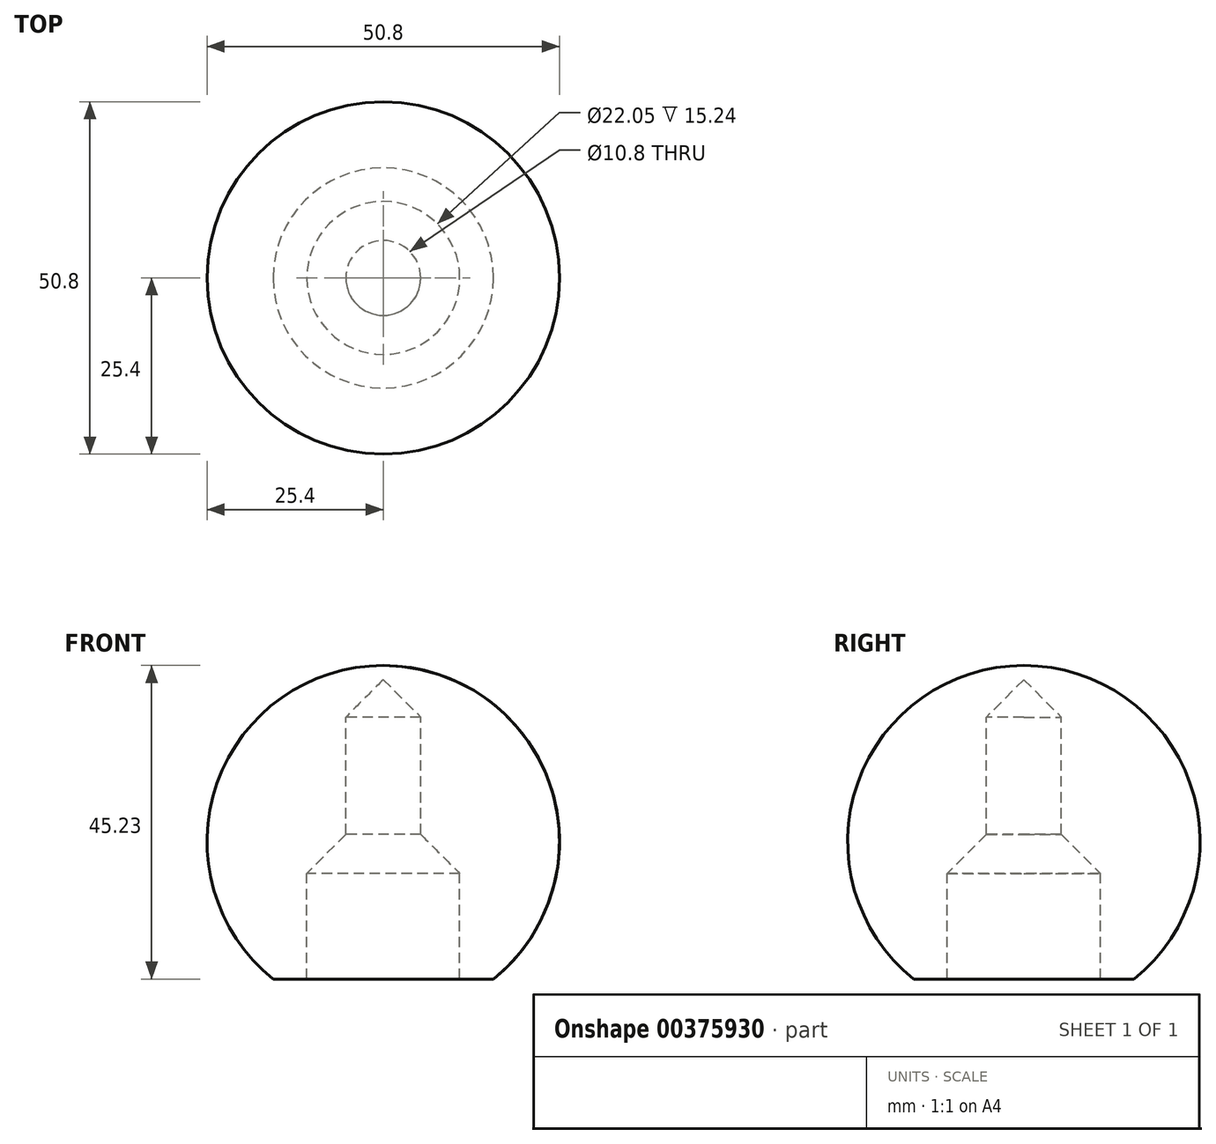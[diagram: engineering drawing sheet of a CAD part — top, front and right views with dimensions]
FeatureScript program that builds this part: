
annotation { "Feature Type Name" : "Feature", "Feature Type Description" : "" }
export const myFeature = defineFeature(function(context is Context, id is Id, definition is map)
    precondition{}
    {
        {
            var Q0;
            Q0=qCreatedBy(makeId("Front.planeOp"),FACE);
            var sketch = newSketch(context, id + "F0", { "sketchPlane" : qUnion([Q0])});
            skLineSegment(sketch, "E0", {"start": v(0, 0) * mm, "end": v(15.88, 0) * mm});
            skLineSegment(sketch, "E1", {"start": v(0, 0) * mm, "end": v(0, 45.23) * mm});
            skArc(sketch, "E2", {"start": v(15.88, 0) * mm, "mid": v(23.97, 28.24) * mm, "end": v(0, 45.23) * mm});
            skSolve(sketch);
        }
        {
            var Q0;
            Q0=makeQuery(id+"F0.imprint","IMPRINT",FACE,{"disambiguationData":[TD([[makeQuery(id+"F0.imprint","IMPRINT",EDGE,{"derivedFrom":sQuery(id+"F0.wireOp",EDGE,"E0")}),1.0]])]});
            var Q1;
            Q1=sQuery(id+"F0.wireOp",EDGE,"E1");
            revolve(context, id + "F1", {"entities" : qUnion([Q0]), "axis" : qUnion([Q1]), "revolveType" : RevolveType.FULL});
        }
        {
            var Q0;
            Q0=qCreatedBy(makeId("Front.planeOp"),FACE);
            var sketch = newSketch(context, id + "F2", { "sketchPlane" : qUnion([Q0])});
            skLineSegment(sketch, "E3", {"start": v(0, 0) * mm, "end": v(0, 43.18) * mm});
            skLineSegment(sketch, "E4", {"start": v(0, 43.18) * mm, "end": v(5.4, 37.78) * mm});
            skLineSegment(sketch, "E5", {"start": v(5.4, 37.78) * mm, "end": v(5.4, 20.86) * mm});
            skLineSegment(sketch, "E6", {"start": v(5.4, 20.86) * mm, "end": v(11.02, 15.24) * mm});
            skLineSegment(sketch, "E7", {"start": v(11.02, 15.24) * mm, "end": v(11.02, 0) * mm});
            skLineSegment(sketch, "E8", {"start": v(11.02, 0) * mm, "end": v(0, 0) * mm});
            skSolve(sketch);
        }
        {
            var Q0;
            Q0 = qSketchRegion(id + "F2", true);
            var Q1;
            Q1=sQuery(id+"F2.wireOp",EDGE,"E3");
            var Q2;
            Q2=sQuery(id+"F2.wireOp",EDGE,"E5");
            var Q3;
            Q3=sQuery(id+"F2.wireOp",EDGE,"E4");
            var Q4;
            Q4=sQuery(id+"F2.wireOp",EDGE,"E6");
            var Q5;
            Q5=sQuery(id+"F2.wireOp",EDGE,"E7");
            var Q6;
            Q6=sQuery(id+"F2.wireOp",EDGE,"E8");
            var Q7;
            Q7=sQuery(id+"F2.wireOp",EDGE,"E3");
            revolve(context, id + "F3", {"operationType" : NewBodyOperationType.REMOVE, "entities" : qUnion([Q0]), "surfaceEntities" : qUnion([Q1, Q2, Q3, Q4, Q5, Q6]), "axis" : qUnion([Q7]), "revolveType" : RevolveType.FULL, "oppositeDirection" : true});
        }
    });
